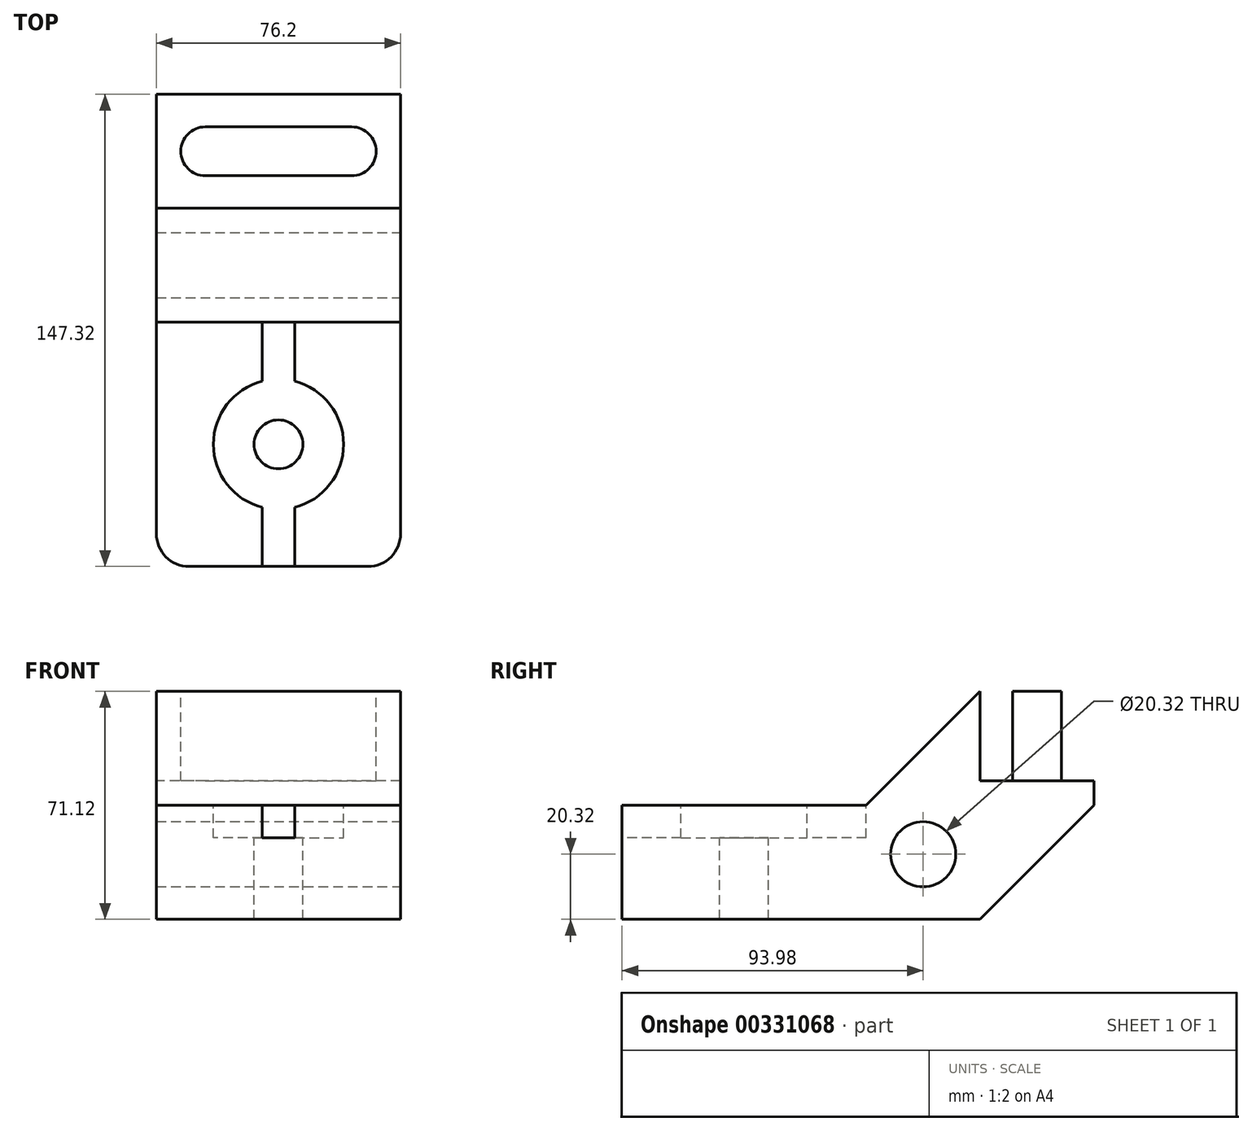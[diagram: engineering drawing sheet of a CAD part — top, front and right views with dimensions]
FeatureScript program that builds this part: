
annotation { "Feature Type Name" : "Feature", "Feature Type Description" : "" }
export const myFeature = defineFeature(function(context is Context, id is Id, definition is map)
    precondition{}
    {
        {
            var Q0;
            Q0=qCreatedBy(makeId("Right.planeOp"),FACE);
            var sketch = newSketch(context, id + "F0", { "sketchPlane" : qUnion([Q0])});
            skLineSegment(sketch, "E0.bottom", {"start": v(0, 0) * mm, "end": v(147.32, 0) * mm});
            skLineSegment(sketch, "E0.top", {"start": v(0, 71.12) * mm, "end": v(147.32, 71.12) * mm});
            skLineSegment(sketch, "E0.left", {"start": v(0, 0) * mm, "end": v(0, 71.12) * mm});
            skLineSegment(sketch, "E0.right", {"start": v(147.32, 0) * mm, "end": v(147.32, 71.12) * mm});
            skSolve(sketch);
        }
        {
            var Q0;
            Q0 = qSketchRegion(id + "F0", true);
            extrude(context, id + "F1", {"entities" : qUnion([Q0]), "depth" : 76.2 * mm});
        }
        {
            var Q0;
            Q0=makeQuery(id+"F1.opExtrude","CAP_FACE",FACE,{"disambiguationData":[OSD([sQuery(id+"F0.wireOp",EDGE,"E0.bottom"),sQuery(id+"F0.wireOp",EDGE,"E0.top"),sQuery(id+"F0.wireOp",EDGE,"E0.left"),sQuery(id+"F0.wireOp",EDGE,"E0.right")])],"isStart":false});
            var sketch = newSketch(context, id + "F2", { "sketchPlane" : qUnion([Q0])});
            skLineSegment(sketch, "E1", {"start": v(0, 0) * mm, "end": v(0, 35.56) * mm});
            skLineSegment(sketch, "E2", {"start": v(0, 35.56) * mm, "end": v(76.2, 35.56) * mm});
            skLineSegment(sketch, "E3", {"start": v(76.2, 35.56) * mm, "end": v(111.76, 71.12) * mm});
            skLineSegment(sketch, "E4", {"start": v(111.76, 71.12) * mm, "end": v(147.32, 71.12) * mm});
            skLineSegment(sketch, "E5", {"start": v(147.32, 71.12) * mm, "end": v(147.32, 35.56) * mm});
            skLineSegment(sketch, "E6", {"start": v(147.32, 35.56) * mm, "end": v(111.76, 0) * mm});
            skLineSegment(sketch, "E7", {"start": v(111.76, 0) * mm, "end": v(0, 0) * mm});
            skSolve(sketch);
        }
        {
            var Q0;
            {var subQ0=sQuery(id+"F2.wireOp",EDGE,"E2");Q0=makeQuery(id+"F2.imprint","IMPRINT",FACE,{"disambiguationData":[TD([[makeQuery(id+"F2.imprint","IMPRINT",EDGE,{"derivedFrom":subQ0}),1.0]])]});}
            var Q1;
            {var subQ0=sQuery(id+"F2.wireOp",EDGE,"E6");Q1=makeQuery(id+"F2.imprint","IMPRINT",FACE,{"disambiguationData":[TD([[makeQuery(id+"F2.imprint","IMPRINT",EDGE,{"derivedFrom":subQ0}),1.0]])]});}
            extrude(context, id + "F3", {"entities" : qUnion([Q0, Q1]), "operationType" : NewBodyOperationType.REMOVE, "endBound" : BoundingType.THROUGH_ALL, "oppositeDirection" : true, "depth" : 25.4 * mm});
        }
        {
            var Q0;
            Q0=makeQuery(id+"F1.opExtrude","SWEPT_FACE",FACE,{"disambiguationData":[OSD([sQuery(id+"F0.wireOp",EDGE,"E0.top")])]});
            var sketch = newSketch(context, id + "F4", { "sketchPlane" : qUnion([Q0])});
            skLineSegment(sketch, "E8", {"start": v(15.24, 129.54) * mm, "end": v(60.96, 129.54) * mm, "construction": true});
            skArc(sketch, "E9.0.startCap", {"start": v(15.24, 121.92) * mm, "mid": v(7.62, 129.54) * mm, "end": v(15.24, 137.16) * mm});
            skArc(sketch, "E9.0.endCap", {"start": v(60.96, 137.16) * mm, "mid": v(68.58, 129.54) * mm, "end": v(60.96, 121.92) * mm});
            skLineSegment(sketch, "E9.0.left", {"start": v(15.24, 137.16) * mm, "end": v(60.96, 137.16) * mm});
            skLineSegment(sketch, "E9.0.right", {"start": v(15.24, 121.92) * mm, "end": v(60.96, 121.92) * mm});
            skSolve(sketch);
        }
        {
            var Q0;
            Q0=makeQuery(id+"F4.imprint","IMPRINT",FACE,{"disambiguationData":[TD([[makeQuery(id+"F4.imprint","IMPRINT",EDGE,{"derivedFrom":sQuery(id+"F4.wireOp",EDGE,"E9.0.startCap")}),-1.0]])]});
            extrude(context, id + "F5", {"entities" : qUnion([Q0]), "operationType" : NewBodyOperationType.REMOVE, "oppositeDirection" : true, "depth" : 27.94 * mm});
        }
        {
            var Q0;
            Q0=makeQuery(id+"F3.boolean.opBoolean","COPY",FACE,{"derivedFrom":makeQuery(id+"F3.opExtrude","SWEPT_FACE",FACE,{"disambiguationData":[OSD([sQuery(id+"F2.wireOp",EDGE,"E2")])]})});
            var sketch = newSketch(context, id + "F6", { "sketchPlane" : qUnion([Q0])});
            skPoint(sketch, "E10", {"position": v(38.1, 38.1) * mm});
            skSolve(sketch);
        }
        {
            var Q0;
            Q0=sQuery(id+"F6.wireOp",VERTEX,"E10");
            var Q1;
            Q1=makeQuery(id+"F1.opExtrude","SWEPT_BODY",BODY,{"disambiguationData":[OSD([sQuery(id+"F0.wireOp",EDGE,"E0.bottom"),sQuery(id+"F0.wireOp",EDGE,"E0.top"),sQuery(id+"F0.wireOp",EDGE,"E0.left"),sQuery(id+"F0.wireOp",EDGE,"E0.right")])]});
            hole(context, id + "F7", {"style" : HoleStyle.C_BORE, "endStyle" : HoleEndStyle.THROUGH, "holeDiameter" : 15.24 * mm, "cBoreDiameter" : 40.64 * mm, "cBoreDepth" : 10.16 * mm, "tappedDepth" : 12.7 * mm, "tapClearance" : 3, "locations" : qUnion([Q0]), "scope" : qUnion([Q1])});
        }
        {
            var Q0;
            Q0=makeQuery(id+"F3.boolean.opBoolean","COPY",FACE,{"derivedFrom":makeQuery(id+"F3.opExtrude","SWEPT_FACE",FACE,{"disambiguationData":[OSD([sQuery(id+"F2.wireOp",EDGE,"E2")])]})});
            var sketch = newSketch(context, id + "F8", { "sketchPlane" : qUnion([Q0])});
            skLineSegment(sketch, "E11.bottom", {"start": v(33.02, 76.2) * mm, "end": v(43.18, 76.2) * mm});
            skLineSegment(sketch, "E11.top", {"start": v(33.02, 0) * mm, "end": v(43.18, 0) * mm});
            skLineSegment(sketch, "E11.left", {"start": v(33.02, 76.2) * mm, "end": v(33.02, 0) * mm});
            skLineSegment(sketch, "E11.right", {"start": v(43.18, 76.2) * mm, "end": v(43.18, 0) * mm});
            skSolve(sketch);
        }
        {
            var Q0;
            {var subQ0=sQuery(id+"F8.wireOp",EDGE,"E11.bottom");Q0=makeQuery(id+"F8.imprint","IMPRINT",FACE,{"disambiguationData":[TD([[makeQuery(id+"F8.imprint","IMPRINT",EDGE,{"derivedFrom":subQ0}),-1.0]])]});}
            var Q1;
            {var subQ0=sQuery(id+"F8.wireOp",EDGE,"E11.top");Q1=makeQuery(id+"F8.imprint","IMPRINT",FACE,{"disambiguationData":[TD([[makeQuery(id+"F8.imprint","IMPRINT",EDGE,{"derivedFrom":subQ0}),1.0]])]});}
            var Q2;
            {var subQ0=sQuery(id+"F8.wireOp",EDGE,"E11.left");var subQ1=makeQuery(id+"F7.hole-0.boolean.opBoolean","COPY",EDGE,{"derivedFrom":makeQuery(id+"F7.hole-0.opRevolve","SWEPT_EDGE",EDGE,{"disambiguationData":[OSD([sQuery(id+"F7.hole-0.sketch.wireOp",EDGE,"cbore_start_line_2"),sQuery(id+"F7.hole-0.sketch.wireOp",EDGE,"cbore_start_line_3")])]})});var subQ2=makeQuery(id+"F8.imprint","INTERSECT",VERTEX,{"disambiguationData":[OD(0.0)],"derivedFrom":[subQ1,subQ0]});Q2=makeQuery(id+"F8.imprint","IMPRINT",FACE,{"disambiguationData":[TD([[makeQuery(id+"F8.imprint","IMPRINT",EDGE,{"disambiguationData":[TD([[subQ2,-1.0]])],"derivedFrom":subQ0}),1.0]])]});}
            extrude(context, id + "F9", {"entities" : qUnion([Q0, Q1, Q2]), "operationType" : NewBodyOperationType.REMOVE, "oppositeDirection" : true, "depth" : 10.16 * mm});
        }
        {
            var Q0;
            Q0=makeQuery(id+"F1.opExtrude","CAP_FACE",FACE,{"disambiguationData":[OSD([sQuery(id+"F0.wireOp",EDGE,"E0.bottom"),sQuery(id+"F0.wireOp",EDGE,"E0.top"),sQuery(id+"F0.wireOp",EDGE,"E0.left"),sQuery(id+"F0.wireOp",EDGE,"E0.right")])],"isStart":false});
            var sketch = newSketch(context, id + "F10", { "sketchPlane" : qUnion([Q0])});
            skPoint(sketch, "E12", {"position": v(93.98, 20.32) * mm});
            skSolve(sketch);
        }
        {
            var Q0;
            Q0=sQuery(id+"F10.wireOp",VERTEX,"E12");
            var Q1;
            Q1=makeQuery(id+"F1.opExtrude","SWEPT_BODY",BODY,{"disambiguationData":[OSD([sQuery(id+"F0.wireOp",EDGE,"E0.bottom"),sQuery(id+"F0.wireOp",EDGE,"E0.top"),sQuery(id+"F0.wireOp",EDGE,"E0.left"),sQuery(id+"F0.wireOp",EDGE,"E0.right")])]});
            hole(context, id + "F11", {"style" : HoleStyle.SIMPLE, "endStyle" : HoleEndStyle.THROUGH, "holeDiameter" : 20.32 * mm, "tappedDepth" : 12.7 * mm, "tapClearance" : 3, "locations" : qUnion([Q0]), "scope" : qUnion([Q1])});
        }
        {
            var Q0;
            Q0=makeQuery(id+"F1.opExtrude","CAP_EDGE",EDGE,{"disambiguationData":[OSD([sQuery(id+"F0.wireOp",EDGE,"E0.left")])],"isStart":true});
            var Q1;
            Q1=makeQuery(id+"F1.opExtrude","CAP_EDGE",EDGE,{"disambiguationData":[OSD([sQuery(id+"F0.wireOp",EDGE,"E0.left")])],"isStart":false});
            fillet(context, id + "F12", {"entities" : qUnion([Q0, Q1]), "radius" : 10.16 * mm, "tangentPropagation" : true, "allowEdgeOverflow" : false});
        }
    });
